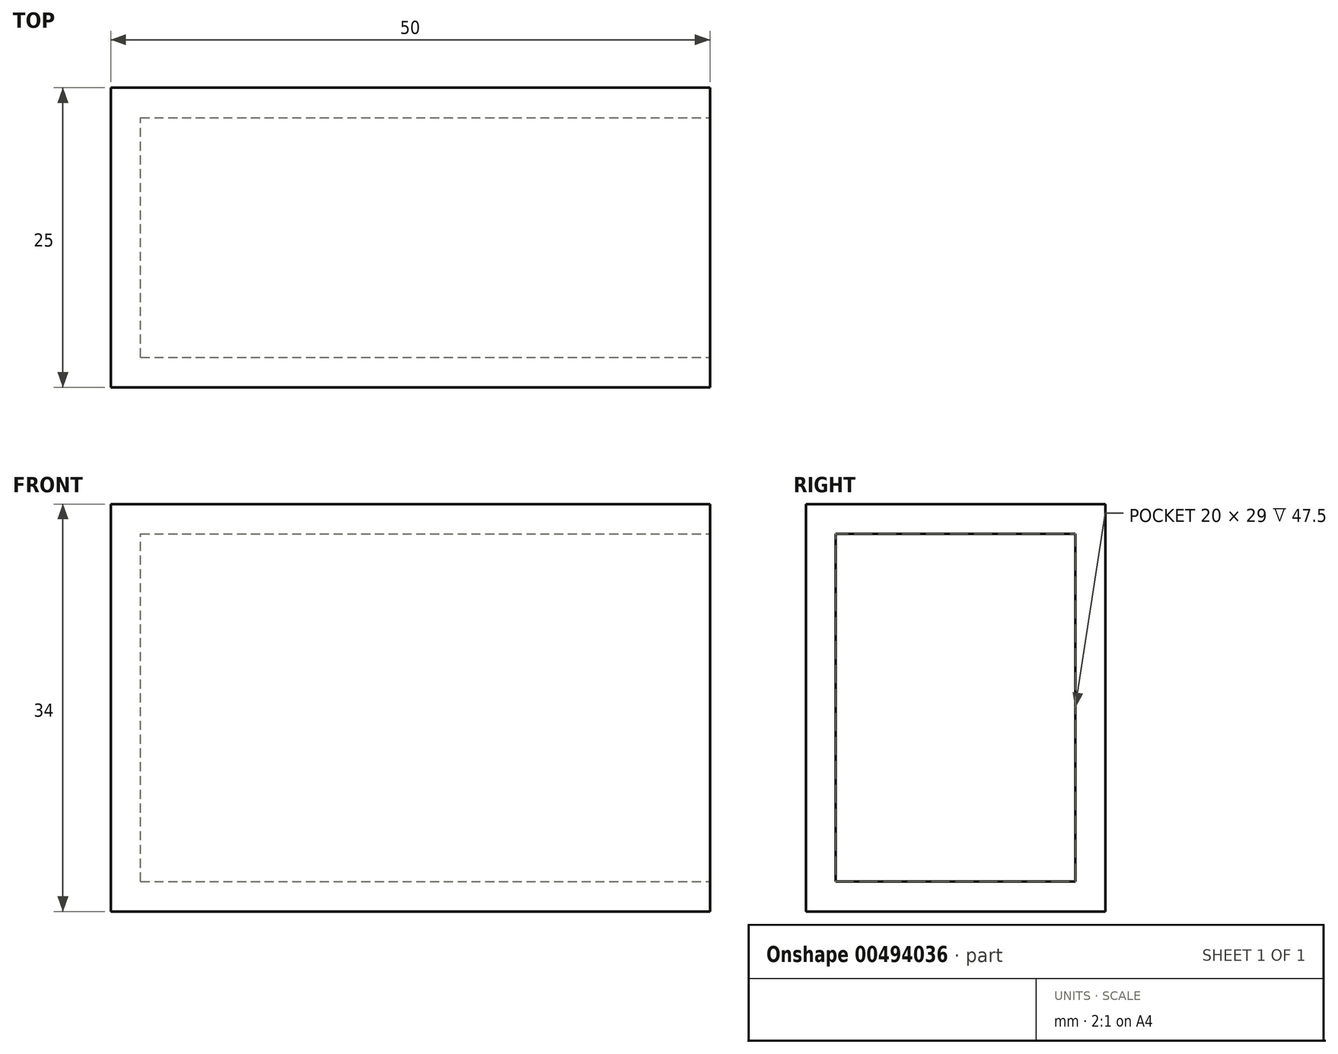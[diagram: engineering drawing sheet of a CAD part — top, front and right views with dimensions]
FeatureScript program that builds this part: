
annotation { "Feature Type Name" : "Feature", "Feature Type Description" : "" }
export const myFeature = defineFeature(function(context is Context, id is Id, definition is map)
    precondition{}
    {
        {
            var Q0;
            Q0=qCreatedBy(makeId("Front.planeOp"),FACE);
            var sketch = newSketch(context, id + "F0", { "sketchPlane" : qUnion([Q0])});
            skLineSegment(sketch, "E0.bottom", {"start": v(-25, -17) * mm, "end": v(25, -17) * mm});
            skLineSegment(sketch, "E0.top", {"start": v(-25, 17) * mm, "end": v(25, 17) * mm});
            skLineSegment(sketch, "E0.left", {"start": v(-25, -17) * mm, "end": v(-25, 17) * mm});
            skLineSegment(sketch, "E0.right", {"start": v(25, -17) * mm, "end": v(25, 17) * mm});
            skPoint(sketch, "E0.middle", {"position": v(0, 0) * mm});
            skSolve(sketch);
        }
        {
            var Q0;
            Q0 = qSketchRegion(id + "F0", true);
            extrude(context, id + "F1", {"entities" : qUnion([Q0]), "depth" : 25 * mm});
        }
        {
            var Q0;
            Q0=makeQuery(id+"F1.opExtrude","SWEPT_FACE",FACE,{"disambiguationData":[OSD([sQuery(id+"F0.wireOp",EDGE,"E0.right")])]});
            shell(context, id + "F2", {"entities" : qUnion([Q0]), "thickness" : 2.5 * mm});
        }
    });
